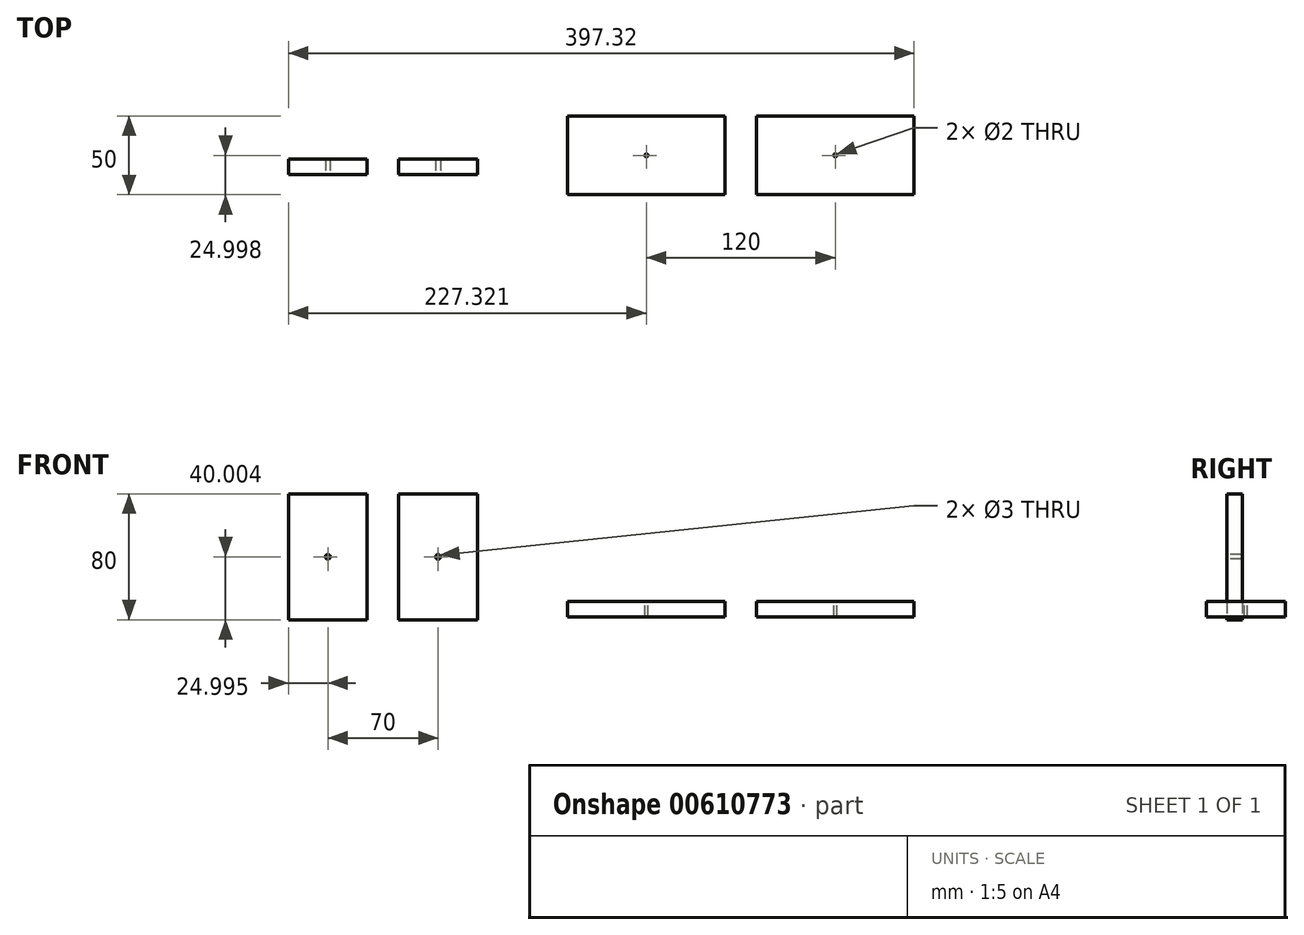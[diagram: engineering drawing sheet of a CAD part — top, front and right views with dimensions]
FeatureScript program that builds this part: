
annotation { "Feature Type Name" : "Feature", "Feature Type Description" : "" }
export const myFeature = defineFeature(function(context is Context, id is Id, definition is map)
    precondition{}
    {
        {
            var Q0;
            Q0=qCreatedBy(makeId("Top.planeOp"),FACE);
            var sketch = newSketch(context, id + "F0", { "sketchPlane" : qUnion([Q0])});
            skLineSegment(sketch, "E0.bottom", {"start": v(-43.75, 27.27) * mm, "end": v(56.25, 27.27) * mm});
            skLineSegment(sketch, "E0.top", {"start": v(-43.75, -22.73) * mm, "end": v(56.25, -22.73) * mm});
            skLineSegment(sketch, "E0.left", {"start": v(-43.75, 27.27) * mm, "end": v(-43.75, -22.73) * mm});
            skLineSegment(sketch, "E0.right", {"start": v(56.25, 27.27) * mm, "end": v(56.25, -22.73) * mm});
            skSolve(sketch);
        }
        {
            var Q0;
            Q0 = qSketchRegion(id + "F0", true);
            extrude(context, id + "F1", {"entities" : qUnion([Q0]), "depth" : 10 * mm, "offsetDistance" : 25 * mm});
        }
        {
            var Q0;
            Q0=makeQuery(id+"F1.opExtrude","CAP_FACE",FACE,{"disambiguationData":[OSD([sQuery(id+"F0.wireOp",EDGE,"E0.bottom"),sQuery(id+"F0.wireOp",EDGE,"E0.top"),sQuery(id+"F0.wireOp",EDGE,"E0.left"),sQuery(id+"F0.wireOp",EDGE,"E0.right")])],"isStart":false});
            var sketch = newSketch(context, id + "F2", { "sketchPlane" : qUnion([Q0])});
            skCircle(sketch, "E1", {"center": v(6.25, 2.27) * mm, "radius": 2.5 * mm});
            skPoint(sketch, "E1.centerSnap0", {"position": v(6.25, 27.27) * mm});
            skPoint(sketch, "E1.centerSnap1", {"position": v(-43.75, 2.27) * mm});
            skSolve(sketch);
        }
        {
            var Q0;
            Q0=sQuery(id+"F2.wireOp",VERTEX,"E1.center");
            var Q1;
            Q1=makeQuery(id+"F1.opExtrude","SWEPT_BODY",BODY,{"disambiguationData":[OSD([sQuery(id+"F0.wireOp",EDGE,"E0.bottom"),sQuery(id+"F0.wireOp",EDGE,"E0.top"),sQuery(id+"F0.wireOp",EDGE,"E0.left"),sQuery(id+"F0.wireOp",EDGE,"E0.right")])]});
            hole(context, id + "F3", {"style" : HoleStyle.SIMPLE, "endStyle" : HoleEndStyle.THROUGH, "holeDiameter" : 2 * mm, "majorDiameter" : 5 * mm, "isTappedThrough" : true, "tappedDepth" : 12 * mm, "tapClearance" : 3, "locations" : qUnion([Q0]), "scope" : qUnion([Q1])});
        }
        {
            var Q0;
            Q0=makeQuery(id+"F1.opExtrude","SWEPT_BODY",BODY,{"disambiguationData":[OSD([sQuery(id+"F0.wireOp",EDGE,"E0.bottom"),sQuery(id+"F0.wireOp",EDGE,"E0.top"),sQuery(id+"F0.wireOp",EDGE,"E0.left"),sQuery(id+"F0.wireOp",EDGE,"E0.right")])]});
            transform(context, id + "F4", {"entities" : qUnion([Q0]), "transformType" : TransformType.TRANSLATION_3D, "dx" : 120 * mm, "dy" : 0 * mm, "dz" : 0 * mm, "makeCopy" : true});
        }
        {
            var Q0;
            Q0=qCreatedBy(makeId("Front.planeOp"),FACE);
            var sketch = newSketch(context, id + "F5", { "sketchPlane" : qUnion([Q0])});
            skLineSegment(sketch, "E2.bottom", {"start": v(-221.07, 78.3) * mm, "end": v(-171.07, 78.3) * mm});
            skLineSegment(sketch, "E2.top", {"start": v(-221.07, -1.7) * mm, "end": v(-171.07, -1.7) * mm});
            skLineSegment(sketch, "E2.left", {"start": v(-221.07, 78.3) * mm, "end": v(-221.07, -1.7) * mm});
            skLineSegment(sketch, "E2.right", {"start": v(-171.07, 78.3) * mm, "end": v(-171.07, -1.7) * mm});
            skSolve(sketch);
        }
        {
            var Q0;
            Q0=makeQuery(id+"F5.imprint","IMPRINT",FACE,{"disambiguationData":[TD([[makeQuery(id+"F5.imprint","IMPRINT",EDGE,{"derivedFrom":sQuery(id+"F5.wireOp",EDGE,"E2.bottom")}),-1.0]])]});
            extrude(context, id + "F6", {"entities" : qUnion([Q0]), "depth" : 10 * mm, "offsetDistance" : 25 * mm});
        }
        {
            var Q0;
            Q0=makeQuery(id+"F6.opExtrude","CAP_FACE",FACE,{"disambiguationData":[OSD([sQuery(id+"F5.wireOp",EDGE,"E2.bottom"),sQuery(id+"F5.wireOp",EDGE,"E2.top"),sQuery(id+"F5.wireOp",EDGE,"E2.left"),sQuery(id+"F5.wireOp",EDGE,"E2.right")])],"isStart":false});
            var sketch = newSketch(context, id + "F7", { "sketchPlane" : qUnion([Q0])});
            skCircle(sketch, "E3", {"center": v(-196.07, 38.3) * mm, "radius": 2.5 * mm});
            skPoint(sketch, "E3.centerSnap0", {"position": v(-196.07, 78.3) * mm});
            skPoint(sketch, "E3.centerSnap1", {"position": v(-221.07, 38.3) * mm});
            skSolve(sketch);
        }
        {
            var Q0;
            Q0=sQuery(id+"F7.wireOp",VERTEX,"E3.center");
            var Q1;
            Q1=makeQuery(id+"F6.opExtrude","SWEPT_BODY",BODY,{"disambiguationData":[OSD([sQuery(id+"F5.wireOp",EDGE,"E2.bottom"),sQuery(id+"F5.wireOp",EDGE,"E2.top"),sQuery(id+"F5.wireOp",EDGE,"E2.left"),sQuery(id+"F5.wireOp",EDGE,"E2.right")])]});
            hole(context, id + "F8", {"style" : HoleStyle.SIMPLE, "endStyle" : HoleEndStyle.THROUGH, "holeDiameter" : 3 * mm, "majorDiameter" : 5 * mm, "isTappedThrough" : true, "tappedDepth" : 12 * mm, "tapClearance" : 3, "locations" : qUnion([Q0]), "scope" : qUnion([Q1])});
        }
        {
            var Q0;
            Q0=makeQuery(id+"F6.opExtrude","SWEPT_BODY",BODY,{"disambiguationData":[OSD([sQuery(id+"F5.wireOp",EDGE,"E2.bottom"),sQuery(id+"F5.wireOp",EDGE,"E2.top"),sQuery(id+"F5.wireOp",EDGE,"E2.left"),sQuery(id+"F5.wireOp",EDGE,"E2.right")])]});
            transform(context, id + "F9", {"entities" : qUnion([Q0]), "transformType" : TransformType.TRANSLATION_3D, "dx" : 70 * mm, "dy" : 0 * mm, "dz" : 0 * mm, "makeCopy" : true});
        }
    });
